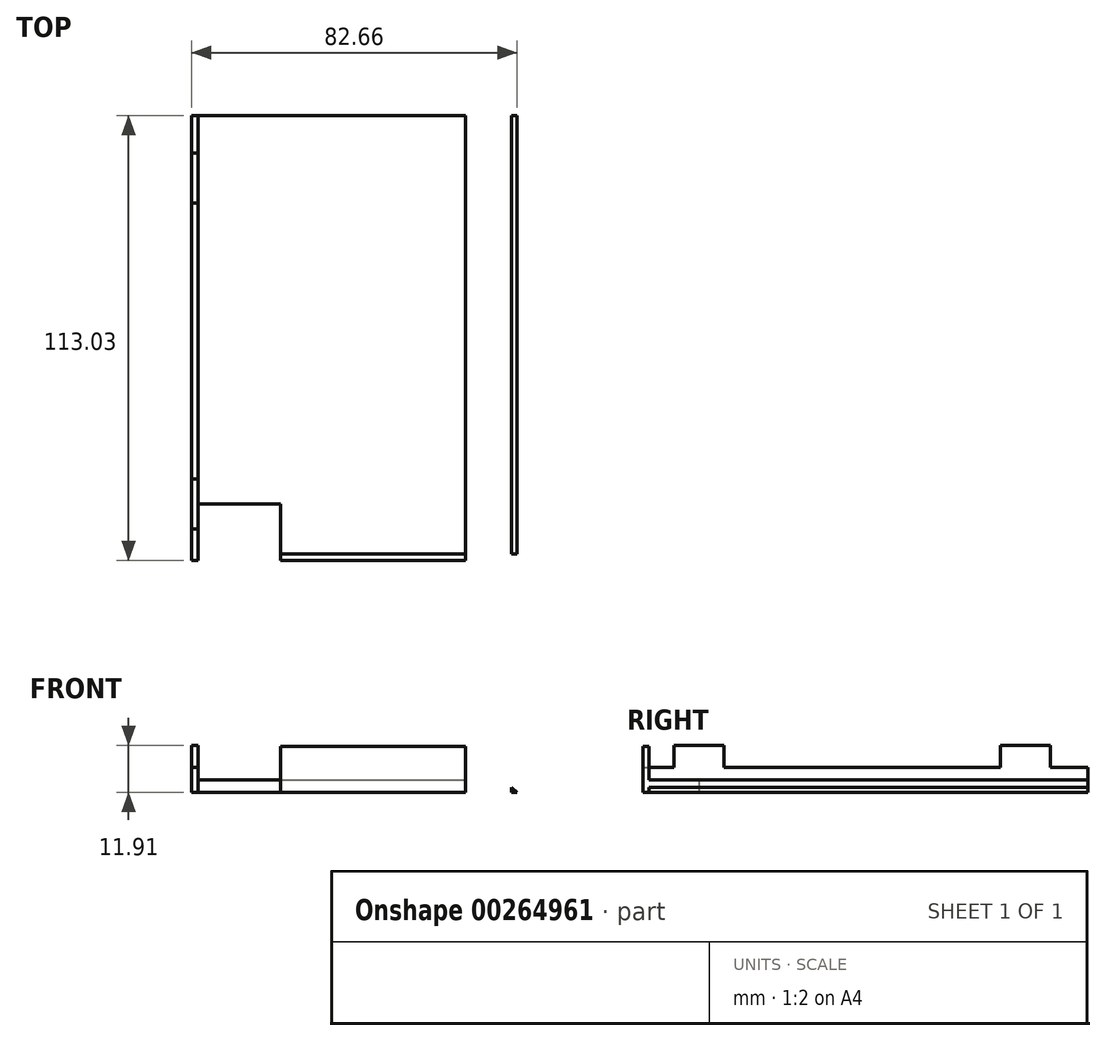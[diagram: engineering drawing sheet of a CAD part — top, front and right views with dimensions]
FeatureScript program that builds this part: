
annotation { "Feature Type Name" : "Feature", "Feature Type Description" : "" }
export const myFeature = defineFeature(function(context is Context, id is Id, definition is map)
    precondition{}
    {
        {
            var Q0;
            Q0=qCreatedBy(makeId("Top.planeOp"),FACE);
            var sketch = newSketch(context, id + "F0", { "sketchPlane" : qUnion([Q0])});
            skLineSegment(sketch, "E0.top", {"start": v(-36.5, -61.91) * mm, "end": v(-34.91, -61.91) * mm});
            skLineSegment(sketch, "E0.left", {"start": v(-36.5, 49.53) * mm, "end": v(-36.5, -6.67) * mm});
            skPoint(sketch, "E0.middle", {"position": v(0, -10.8) * mm});
            skLineSegment(sketch, "E1", {"start": v(-34.91, -61.91) * mm, "end": v(-34.91, -18.44) * mm});
            skLineSegment(sketch, "E2", {"start": v(44.73, -61.91) * mm, "end": v(33.06, -61.91) * mm});
            skLineSegment(sketch, "E3", {"start": v(33.06, -52.15) * mm, "end": v(33.06, -61.91) * mm});
            skLineSegment(sketch, "E4", {"start": v(33.06, -52.15) * mm, "end": v(33.06, -18.44) * mm});
            skLineSegment(sketch, "E5", {"start": v(-36.5, 49.53) * mm, "end": v(2.98, 49.53) * mm});
            skLineSegment(sketch, "E6", {"start": v(2.98, 49.53) * mm, "end": v(2.98, 51.12) * mm});
            skLineSegment(sketch, "E7", {"start": v(-36.5, -61.91) * mm, "end": v(-36.5, -55.56) * mm});
            skLineSegment(sketch, "E8", {"start": v(-36.5, -55.56) * mm, "end": v(-34.91, -55.56) * mm});
            skLineSegment(sketch, "E9", {"start": v(-36.5, -55.56) * mm, "end": v(-36.5, -52.39) * mm});
            skLineSegment(sketch, "E10", {"start": v(-36.5, -52.39) * mm, "end": v(-34.91, -52.39) * mm});
            skLineSegment(sketch, "E11", {"start": v(-34.91, -52.39) * mm, "end": v(-34.91, -55.56) * mm});
            skLineSegment(sketch, "E12", {"start": v(-36.5, 49.53) * mm, "end": v(-36.5, 40) * mm});
            skLineSegment(sketch, "E13", {"start": v(-36.5, 40) * mm, "end": v(-34.91, 40) * mm});
            skLineSegment(sketch, "E14", {"start": v(-34.91, 40) * mm, "end": v(-34.91, 36.83) * mm});
            skLineSegment(sketch, "E15", {"start": v(-34.94, 36.83) * mm, "end": v(-36.5, 36.83) * mm});
            skLineSegment(sketch, "E16", {"start": v(-36.5, 36.83) * mm, "end": v(-34.94, 36.83) * mm});
            skLineSegment(sketch, "E17.bottom", {"start": v(-36.5, -52.39) * mm, "end": v(-35.83, -52.39) * mm});
            skLineSegment(sketch, "E17.top", {"start": v(-35.83, -55.56) * mm, "end": v(-34.91, -55.56) * mm});
            skLineSegment(sketch, "E17.left", {"start": v(-35.83, -52.39) * mm, "end": v(-35.83, -55.56) * mm});
            skLineSegment(sketch, "E18.bottom", {"start": v(-35.72, 36.83) * mm, "end": v(-34.94, 36.83) * mm});
            skLineSegment(sketch, "E18.top", {"start": v(-35.72, 40) * mm, "end": v(-34.91, 40) * mm});
            skLineSegment(sketch, "E18.left", {"start": v(-35.72, 36.83) * mm, "end": v(-35.72, 40) * mm});
            skLineSegment(sketch, "E19.left", {"start": v(-35.83, -54.55) * mm, "end": v(-35.83, -53.37) * mm});
            skLineSegment(sketch, "E20.left", {"start": v(-35.72, 37.85) * mm, "end": v(-35.72, 38.9) * mm});
            skPoint(sketch, "E21.orphan", {"position": v(-32.54, -52.39) * mm});
            skPoint(sketch, "E22.start.orphan", {"position": v(-34.94, 36.83) * mm});
            skPoint(sketch, "E23.orphan", {"position": v(-32.54, 40) * mm});
            skPoint(sketch, "E24.orphan", {"position": v(32.06, 51.12) * mm});
            skLineSegment(sketch, "E25.trimOffspring", {"start": v(33.06, -61.91) * mm, "end": v(44.73, -61.91) * mm});
            skPoint(sketch, "E26.end.orphan", {"position": v(36.82, 51.12) * mm});
            skPoint(sketch, "E27.end.orphan", {"position": v(38.4, -61.91) * mm});
            skLineSegment(sketch, "E28", {"start": v(-34.91, 33.66) * mm, "end": v(-36.5, 33.66) * mm});
            skPoint(sketch, "E29.start.orphan", {"position": v(-32.54, 36.83) * mm});
            skLineSegment(sketch, "E30.MirrorCS", {"start": v(-36.5, -49.21) * mm, "end": v(-34.09, -49.21) * mm});
            skLineSegment(sketch, "E31", {"start": v(32.8, 3.5) * mm, "end": v(33.06, 3.5) * mm});
            skLineSegment(sketch, "E32", {"start": v(32.8, -1.27) * mm, "end": v(33.06, -1.27) * mm});
            skLineSegment(sketch, "E33", {"start": v(32.8, -23.81) * mm, "end": v(33.06, -23.81) * mm});
            skLineSegment(sketch, "E34", {"start": v(32.8, -28.57) * mm, "end": v(33.06, -28.57) * mm});
            skPoint(sketch, "E35.end.orphan", {"position": v(47.28, 51.12) * mm});
            skLineSegment(sketch, "E36", {"start": v(-36.5, 33.66) * mm, "end": v(-36.5, 27.3) * mm});
            skLineSegment(sketch, "E37", {"start": v(-36.5, 27.3) * mm, "end": v(-34.91, 27.3) * mm});
            skLineSegment(sketch, "E38", {"start": v(-36.5, -49.21) * mm, "end": v(-36.5, -42.86) * mm});
            skLineSegment(sketch, "E39", {"start": v(-36.5, -42.86) * mm, "end": v(-34.91, -42.86) * mm});
            skLineSegment(sketch, "E40", {"start": v(44.73, -61.91) * mm, "end": v(46.16, -61.91) * mm});
            skLineSegment(sketch, "E41", {"start": v(44.73, -61.91) * mm, "end": v(44.73, -18.44) * mm});
            skLineSegment(sketch, "E42", {"start": v(44.73, 49.53) * mm, "end": v(44.73, -6.67) * mm});
            skLineSegment(sketch, "E43.trimOffspring", {"start": v(-36.5, -6.67) * mm, "end": v(-36.5, -11.93) * mm});
            skLineSegment(sketch, "E44.trimOffspring", {"start": v(-34.91, -6.67) * mm, "end": v(-34.91, 49.53) * mm});
            skLineSegment(sketch, "E45.trimOffspring", {"start": v(33.06, -6.67) * mm, "end": v(33.06, 49.53) * mm});
            skLineSegment(sketch, "E46.trimOffspring", {"start": v(44.73, -6.67) * mm, "end": v(44.73, -11.93) * mm});
            skLineSegment(sketch, "E47.trimOffspring", {"start": v(46.16, -6.67) * mm, "end": v(46.16, 49.53) * mm});
            skLineSegment(sketch, "E48.trimOffspring", {"start": v(44.73, -6.67) * mm, "end": v(44.73, 49.53) * mm});
            skLineSegment(sketch, "E49", {"start": v(2.98, 49.53) * mm, "end": v(9.4, 49.53) * mm});
            skPoint(sketch, "E50.start.orphan", {"position": v(2.98, 36.83) * mm});
            skLineSegment(sketch, "E51.MirrorCS", {"start": v(-36.5, -63.5) * mm, "end": v(-34.91, -63.5) * mm});
            skLineSegment(sketch, "E52.MirrorCS", {"start": v(-36.5, -63.5) * mm, "end": v(-36.5, -61.91) * mm});
            skLineSegment(sketch, "E53.MirrorCS", {"start": v(-34.91, -5.7) * mm, "end": v(-34.91, -11.93) * mm});
            skLineSegment(sketch, "E54.MirrorCS", {"start": v(33.06, -63.5) * mm, "end": v(44.73, -63.5) * mm});
            skLineSegment(sketch, "E55.MirrorCS", {"start": v(46.16, -63.5) * mm, "end": v(44.73, -63.5) * mm});
            skLineSegment(sketch, "E56.MirrorCS", {"start": v(33.06, -5.7) * mm, "end": v(33.06, -11.93) * mm});
            skLineSegment(sketch, "E57.MirrorCS", {"start": v(46.16, 49.53) * mm, "end": v(46.16, -5.7) * mm});
            skLineSegment(sketch, "E58.MirrorCS", {"start": v(46.16, -5.7) * mm, "end": v(46.16, -11.93) * mm});
            skLineSegment(sketch, "E59", {"start": v(2.98, -63.5) * mm, "end": v(9.4, -63.5) * mm});
            skLineSegment(sketch, "E60", {"start": v(-13.86, -61.91) * mm, "end": v(-13.86, -63.5) * mm});
            skLineSegment(sketch, "E61.trimOffspring", {"start": v(-13.86, -63.5) * mm, "end": v(2.98, -63.5) * mm});
            skPoint(sketch, "E62.trimOffspring.start.orphan", {"position": v(2.98, -61.91) * mm});
            skLineSegment(sketch, "E63", {"start": v(-13.86, -61.91) * mm, "end": v(-13.86, -49.21) * mm});
            skLineSegment(sketch, "E64", {"start": v(-13.86, -49.21) * mm, "end": v(-34.09, -49.21) * mm});
            skPoint(sketch, "E65.start.orphan", {"position": v(-32.54, -55.56) * mm});
            skPoint(sketch, "E66.orphan", {"position": v(-34.09, -55.56) * mm});
            skPoint(sketch, "E67.start.orphan", {"position": v(32.26, 36.83) * mm});
            skPoint(sketch, "E68.start.orphan", {"position": v(32.06, -61.91) * mm});
            skLineSegment(sketch, "E69", {"start": v(33.06, 49.53) * mm, "end": v(46.16, 49.53) * mm});
            skPoint(sketch, "E70.orphan", {"position": v(-34.91, 51.12) * mm});
            skPoint(sketch, "E71.end.orphan", {"position": v(44.73, 51.12) * mm});
            skPoint(sketch, "E71.start.orphan", {"position": v(46.16, 51.12) * mm});
            skPoint(sketch, "E72.orphan", {"position": v(-36.5, 51.12) * mm});
            skLineSegment(sketch, "E73", {"start": v(-13.86, -61.91) * mm, "end": v(9.4, -61.91) * mm});
            skLineSegment(sketch, "E74.trimOffspring", {"start": v(-34.91, -11.93) * mm, "end": v(-34.91, -6.67) * mm});
            skLineSegment(sketch, "E75.trimOffspring", {"start": v(-34.91, -18.44) * mm, "end": v(-34.91, -63.5) * mm});
            skLineSegment(sketch, "E76.trimOffspring", {"start": v(-36.5, -18.44) * mm, "end": v(-36.5, -61.91) * mm});
            skLineSegment(sketch, "E77.trimOffspring", {"start": v(33.06, -18.44) * mm, "end": v(33.06, -63.5) * mm});
            skLineSegment(sketch, "E78.trimOffspring", {"start": v(33.06, -11.93) * mm, "end": v(33.06, -6.67) * mm});
            skLineSegment(sketch, "E79.trimOffspring", {"start": v(46.16, -11.93) * mm, "end": v(46.16, -6.67) * mm});
            skLineSegment(sketch, "E80.trimOffspring", {"start": v(44.73, -11.93) * mm, "end": v(44.73, -6.67) * mm});
            skLineSegment(sketch, "E81.trimOffspring", {"start": v(46.16, -18.44) * mm, "end": v(46.16, -63.5) * mm});
            skLineSegment(sketch, "E82.trimOffspring", {"start": v(44.73, -18.44) * mm, "end": v(44.73, -61.91) * mm});
            skLineSegment(sketch, "E83.trimOffspring", {"start": v(25.15, 49.53) * mm, "end": v(33.06, 49.53) * mm});
            skLineSegment(sketch, "E84.trimOffspring", {"start": v(25.15, -61.91) * mm, "end": v(33.06, -61.91) * mm});
            skLineSegment(sketch, "E85.trimOffspring", {"start": v(25.15, -63.5) * mm, "end": v(33.06, -63.5) * mm});
            skLineSegment(sketch, "E86.bottom", {"start": v(9.4, -63.5) * mm, "end": v(25.15, -63.5) * mm});
            skLineSegment(sketch, "E86.top", {"start": v(9.4, 49.53) * mm, "end": v(25.15, 49.53) * mm});
            skLineSegment(sketch, "E87", {"start": v(25.15, -61.91) * mm, "end": v(9.4, -61.91) * mm});
            skLineSegment(sketch, "E88", {"start": v(46.16, -11.93) * mm, "end": v(46.16, -18.44) * mm});
            skLineSegment(sketch, "E89", {"start": v(44.73, -11.93) * mm, "end": v(44.73, -18.44) * mm});
            skLineSegment(sketch, "E90", {"start": v(-34.91, -11.93) * mm, "end": v(-34.91, -18.44) * mm});
            skLineSegment(sketch, "E91", {"start": v(-36.5, -11.93) * mm, "end": v(-36.5, -18.44) * mm});
            skLineSegment(sketch, "E92", {"start": v(33.06, -11.93) * mm, "end": v(33.06, -18.44) * mm});
            skSolve(sketch);
        }
        {
            var Q0;
            {var subQ2=sQuery(id+"F0.wireOp",EDGE,"E49");Q0=makeQuery(id+"F0.imprint","IMPRINT",FACE,{"disambiguationData":[TD([[makeQuery(id+"F0.imprint","IMPRINT",EDGE,{"derivedFrom":subQ2}),-1.0]])]});}
            extrude(context, id + "F1", {"entities" : qUnion([Q0]), "depth" : 3.17 * mm, "offsetDistance" : 25.4 * mm});
        }
        {
            var Q0;
            {var subQ2=sQuery(id+"F0.wireOp",EDGE,"E14");Q0=makeQuery(id+"F0.imprint","IMPRINT",FACE,{"disambiguationData":[TD([[makeQuery(id+"F0.imprint","IMPRINT",EDGE,{"derivedFrom":subQ2}),-1.0]])]});}
            var Q1;
            {var subQ0=sQuery(id+"F0.wireOp",EDGE,"E10");Q1=makeQuery(id+"F0.imprint","IMPRINT",FACE,{"disambiguationData":[TD([[makeQuery(id+"F0.imprint","IMPRINT",EDGE,{"derivedFrom":subQ0}),1.0]])]});}
            var Q2;
            {var subQ0=sQuery(id+"F0.wireOp",EDGE,"E9");Q2=makeQuery(id+"F0.imprint","IMPRINT",FACE,{"disambiguationData":[TD([[makeQuery(id+"F0.imprint","IMPRINT",EDGE,{"derivedFrom":subQ0}),-1.0]])]});}
            var Q3;
            {var subQ4=sQuery(id+"F0.wireOp",EDGE,"E10");Q3=makeQuery(id+"F0.imprint","IMPRINT",FACE,{"disambiguationData":[TD([[makeQuery(id+"F0.imprint","IMPRINT",EDGE,{"derivedFrom":subQ4}),-1.0]])]});}
            var Q4;
            {var subQ3=sQuery(id+"F0.wireOp",EDGE,"E13");Q4=makeQuery(id+"F0.imprint","IMPRINT",FACE,{"disambiguationData":[TD([[makeQuery(id+"F0.imprint","IMPRINT",EDGE,{"derivedFrom":subQ3}),-1.0]])]});}
            var Q5;
            {var subQ0=sQuery(id+"F0.wireOp",EDGE,"E28");Q5=makeQuery(id+"F0.imprint","IMPRINT",FACE,{"disambiguationData":[TD([[makeQuery(id+"F0.imprint","IMPRINT",EDGE,{"derivedFrom":subQ0}),1.0]])]});}
            var Q6;
            {var subQ4=sQuery(id+"F0.wireOp",EDGE,"E38");Q6=makeQuery(id+"F0.imprint","IMPRINT",FACE,{"disambiguationData":[TD([[makeQuery(id+"F0.imprint","IMPRINT",EDGE,{"derivedFrom":subQ4}),-1.0]])]});}
            var Q7;
            {var subQ1=sQuery(id+"F0.wireOp",EDGE,"E16");Q7=makeQuery(id+"F0.imprint","IMPRINT",FACE,{"disambiguationData":[TD([[makeQuery(id+"F0.imprint","IMPRINT",EDGE,{"derivedFrom":subQ1}),-1.0]])]});}
            var Q8;
            {var subQ0=sQuery(id+"F0.wireOp",EDGE,"E39");Q8=makeQuery(id+"F0.imprint","IMPRINT",FACE,{"disambiguationData":[TD([[makeQuery(id+"F0.imprint","IMPRINT",EDGE,{"derivedFrom":subQ0}),-1.0]])]});}
            var Q9;
            {var subQ1=sQuery(id+"F0.wireOp",EDGE,"E8");Q9=makeQuery(id+"F0.imprint","IMPRINT",FACE,{"disambiguationData":[TD([[makeQuery(id+"F0.imprint","IMPRINT",EDGE,{"derivedFrom":subQ1}),1.0]])]});}
            extrude(context, id + "F2", {"entities" : qUnion([Q0, Q1, Q2, Q3, Q4, Q5, Q6, Q7, Q8, Q9]), "operationType" : NewBodyOperationType.ADD, "depth" : 11.9 * mm});
        }
        {
            var Q0;
            {var subQ0=sQuery(id+"F0.wireOp",EDGE,"E13");Q0=makeQuery(id+"F0.imprint","IMPRINT",FACE,{"disambiguationData":[TD([[makeQuery(id+"F0.imprint","IMPRINT",EDGE,{"derivedFrom":subQ0}),1.0]])]});}
            var Q1;
            {var subQ0=sQuery(id+"F0.wireOp",EDGE,"E37");Q1=makeQuery(id+"F0.imprint","IMPRINT",FACE,{"disambiguationData":[TD([[makeQuery(id+"F0.imprint","IMPRINT",EDGE,{"derivedFrom":subQ0}),-1.0]])]});}
            var Q2;
            {var subQ1=sQuery(id+"F0.wireOp",EDGE,"E7");Q2=makeQuery(id+"F0.imprint","IMPRINT",FACE,{"disambiguationData":[TD([[makeQuery(id+"F0.imprint","IMPRINT",EDGE,{"derivedFrom":subQ1}),-1.0]])]});}
            var Q3;
            {var subQ0=sQuery(id+"F0.wireOp",EDGE,"E39");Q3=makeQuery(id+"F0.imprint","IMPRINT",FACE,{"disambiguationData":[TD([[makeQuery(id+"F0.imprint","IMPRINT",EDGE,{"derivedFrom":subQ0}),-1.0]])]});}
            var Q4;
            {var subQ0=sQuery(id+"F0.wireOp",EDGE,"E8");Q4=makeQuery(id+"F0.imprint","IMPRINT",FACE,{"disambiguationData":[TD([[makeQuery(id+"F0.imprint","IMPRINT",EDGE,{"derivedFrom":subQ0}),-1.0]])]});}
            var Q5;
            {var subQ0=sQuery(id+"F0.wireOp",EDGE,"E51.MirrorCS");Q5=makeQuery(id+"F0.imprint","IMPRINT",FACE,{"disambiguationData":[TD([[makeQuery(id+"F0.imprint","IMPRINT",EDGE,{"derivedFrom":subQ0}),1.0]])]});}
            extrude(context, id + "F3", {"entities" : qUnion([Q0, Q1, Q2, Q3, Q4, Q5]), "operationType" : NewBodyOperationType.ADD, "depth" : 6.35 * mm, "offsetDistance" : 25.4 * mm});
        }
        {
            var Q0;
            {var subQ7=sQuery(id+"F0.wireOp",EDGE,"E25.trimOffspring");Q0=makeQuery(id+"F0.imprint","IMPRINT",FACE,{"disambiguationData":[TD([[makeQuery(id+"F0.imprint","IMPRINT",EDGE,{"derivedFrom":subQ7}),1.0]])]});}
            var Q1;
            {var subQ2=sQuery(id+"F0.wireOp",EDGE,"E40");Q1=makeQuery(id+"F0.imprint","IMPRINT",FACE,{"disambiguationData":[TD([[makeQuery(id+"F0.imprint","IMPRINT",EDGE,{"derivedFrom":subQ2}),1.0]])]});}
            var Q2;
            {var subQ2=sQuery(id+"F0.wireOp",EDGE,"E25.trimOffspring");Q2=makeQuery(id+"F0.imprint","IMPRINT",FACE,{"disambiguationData":[TD([[makeQuery(id+"F0.imprint","IMPRINT",EDGE,{"derivedFrom":subQ2}),-1.0]])]});}
            extrude(context, id + "F4", {"entities" : qUnion([Q0, Q1, Q2]), "operationType" : NewBodyOperationType.ADD, "depth" : 11.68 * mm, "offsetDistance" : 25.4 * mm});
        }
        {
            var Q0;
            Q0=makeQuery(id+"F4.opExtrude","CAP_EDGE",EDGE,{"disambiguationData":[OSD([sQuery(id+"F0.wireOp",EDGE,"E57.MirrorCS"),sQuery(id+"F0.wireOp",EDGE,"E58.MirrorCS")])],"isStart":false});
            chamfer(context, id + "F5", {"entities" : qUnion([Q0]), "chamferType" : ChamferType.TWO_OFFSETS, "width1" : 11.67 * mm, "oppositeDirection" : false, "width2" : 13.1 * mm, "tangentPropagation" : true});
        }
        {
            var Q0;
            {var subQ0=sQuery(id+"F0.wireOp",EDGE,"E59");Q0=makeQuery(id+"F0.imprint","IMPRINT",FACE,{"disambiguationData":[TD([[makeQuery(id+"F0.imprint","IMPRINT",EDGE,{"derivedFrom":subQ0}),1.0]])]});}
            extrude(context, id + "F6", {"entities" : qUnion([Q0]), "operationType" : NewBodyOperationType.ADD, "depth" : 11.68 * mm, "offsetDistance" : 25.4 * mm});
        }
    });
